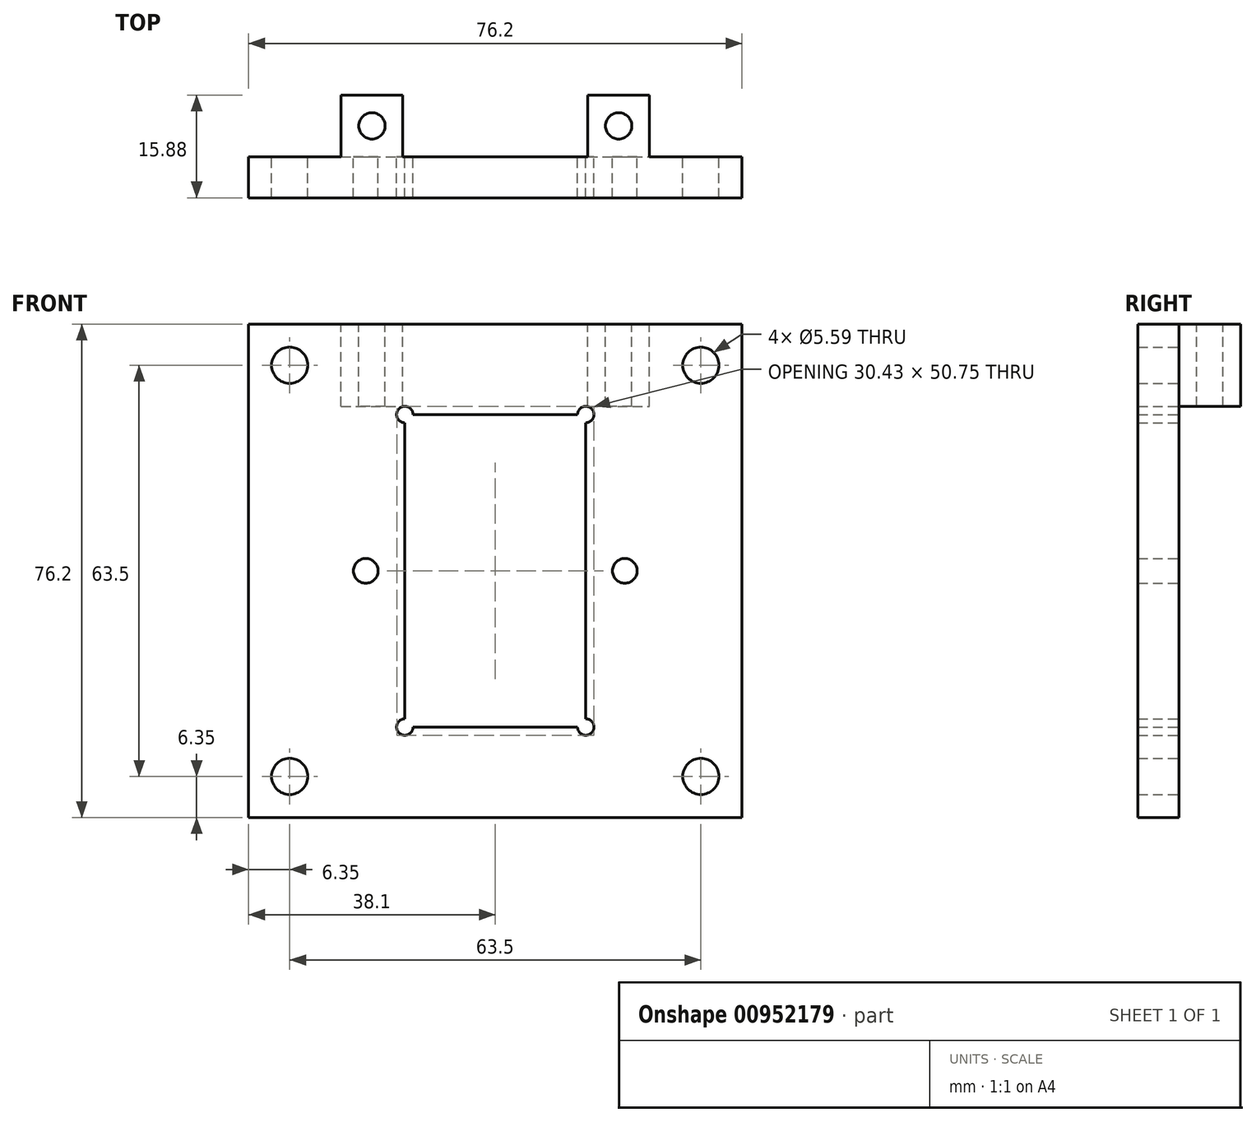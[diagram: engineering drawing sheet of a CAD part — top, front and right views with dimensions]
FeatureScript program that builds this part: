
annotation { "Feature Type Name" : "Feature", "Feature Type Description" : "" }
export const myFeature = defineFeature(function(context is Context, id is Id, definition is map)
    precondition{}
    {
        {
            var Q0;
            Q0=qCreatedBy(makeId("Front.planeOp"),FACE);
            var sketch = newSketch(context, id + "F0", { "sketchPlane" : qUnion([Q0])});
            skLineSegment(sketch, "E0.bottom", {"start": v(39.15, -38.1) * mm, "end": v(38.1, -38.1) * mm});
            skLineSegment(sketch, "E0.top", {"start": v(-38.1, 38.1) * mm, "end": v(38.1, 38.1) * mm});
            skLineSegment(sketch, "E0.right", {"start": v(38.1, -38.1) * mm, "end": v(38.1, 38.1) * mm});
            skLineSegment(sketch, "E1", {"start": v(-38.1, 38.1) * mm, "end": v(-38.1, -38.1) * mm});
            skLineSegment(sketch, "E2", {"start": v(38.1, -38.1) * mm, "end": v(-38.1, -38.1) * mm});
            skSolve(sketch);
        }
        {
            var Q0;
            Q0=qCreatedBy(makeId("Front.planeOp"),FACE);
            var sketch = newSketch(context, id + "F1", { "sketchPlane" : qUnion([Q0])});
            skLineSegment(sketch, "E3.bottom", {"start": v(-12.7, 24.13) * mm, "end": v(12.7, 24.13) * mm});
            skLineSegment(sketch, "E3.top", {"start": v(-12.7, -24.13) * mm, "end": v(12.7, -24.13) * mm});
            skLineSegment(sketch, "E3.left", {"start": v(-13.97, 22.86) * mm, "end": v(-13.97, -22.86) * mm});
            skLineSegment(sketch, "E3.right", {"start": v(13.97, 22.86) * mm, "end": v(13.97, -22.86) * mm});
            skArc(sketch, "E4", {"start": v(-12.7, 24.13) * mm, "mid": v(-14.87, 25.03) * mm, "end": v(-13.97, 22.86) * mm});
            skArc(sketch, "E5", {"start": v(13.97, 22.86) * mm, "mid": v(14.87, 25.03) * mm, "end": v(12.7, 24.13) * mm});
            skArc(sketch, "E6", {"start": v(-13.97, -22.86) * mm, "mid": v(-14.87, -25.03) * mm, "end": v(-12.7, -24.13) * mm});
            skArc(sketch, "E7", {"start": v(12.7, -24.13) * mm, "mid": v(14.87, -25.03) * mm, "end": v(13.97, -22.86) * mm});
            skSolve(sketch);
        }
        {
            var Q0;
            Q0=qCreatedBy(makeId("Front.planeOp"),FACE);
            var sketch = newSketch(context, id + "F2", { "sketchPlane" : qUnion([Q0])});
            skCircle(sketch, "E8", {"center": v(-31.75, 31.75) * mm, "radius": 2.8 * mm});
            skCircle(sketch, "E9", {"center": v(-31.75, -31.75) * mm, "radius": 2.8 * mm});
            skCircle(sketch, "E10", {"center": v(31.75, -31.75) * mm, "radius": 2.8 * mm});
            skCircle(sketch, "E11", {"center": v(31.75, 31.75) * mm, "radius": 2.8 * mm});
            skSolve(sketch);
        }
        {
            var Q0;
            Q0=qSketchRegion(id+"F0",true);
            extrude(context, id + "F3", {"entities" : qUnion([Q0]), "depth" : 6.35 * mm, "offsetDistance" : 25.4 * mm});
        }
        {
            var Q0;
            Q0=qSketchRegion(id+"F1",true);
            extrude(context, id + "F4", {"entities" : qUnion([Q0]), "operationType" : NewBodyOperationType.REMOVE, "endBound" : BoundingType.THROUGH_ALL, "depth" : 25.4 * mm, "offsetDistance" : 25.4 * mm});
        }
        {
            var Q0;
            Q0=qSketchRegion(id+"F2",true);
            extrude(context, id + "F5", {"entities" : qUnion([Q0]), "operationType" : NewBodyOperationType.REMOVE, "endBound" : BoundingType.THROUGH_ALL, "depth" : 25.4 * mm, "offsetDistance" : 25.4 * mm});
        }
        {
            var Q0;
            Q0=makeQuery(id+"F3.opExtrude","SWEPT_FACE",FACE,{"disambiguationData":[OSD([sQuery(id+"F0.wireOp",EDGE,"E0.top")])]});
            var sketch = newSketch(context, id + "F6", { "sketchPlane" : qUnion([Q0])});
            skLineSegment(sketch, "E12.bottom", {"start": v(-23.81, 0) * mm, "end": v(-14.29, 0) * mm});
            skLineSegment(sketch, "E12.top", {"start": v(-23.81, 9.53) * mm, "end": v(-14.29, 9.53) * mm});
            skLineSegment(sketch, "E12.left", {"start": v(-23.81, 0) * mm, "end": v(-23.81, 9.53) * mm});
            skLineSegment(sketch, "E12.right", {"start": v(-14.29, 0) * mm, "end": v(-14.29, 9.52) * mm});
            skLineSegment(sketch, "E13.bottom", {"start": v(23.81, 0) * mm, "end": v(14.29, 0) * mm});
            skLineSegment(sketch, "E13.top", {"start": v(23.81, 9.53) * mm, "end": v(14.29, 9.52) * mm});
            skLineSegment(sketch, "E13.left", {"start": v(23.81, 0) * mm, "end": v(23.81, 9.53) * mm});
            skLineSegment(sketch, "E13.right", {"start": v(14.29, 0) * mm, "end": v(14.29, 9.52) * mm});
            skCircle(sketch, "E14", {"center": v(-19.05, 4.76) * mm, "radius": 2.03 * mm});
            skCircle(sketch, "E15", {"center": v(19.05, 4.76) * mm, "radius": 2.03 * mm});
            skSolve(sketch);
        }
        {
            var Q0;
            Q0=qSketchRegion(id+"F6",true);
            extrude(context, id + "F7", {"entities" : qUnion([Q0]), "operationType" : NewBodyOperationType.ADD, "oppositeDirection" : true, "depth" : 12.7 * mm, "offsetDistance" : 25.4 * mm});
        }
        {
            var Q0;
            Q0=qCreatedBy(makeId("Front.planeOp"),FACE);
            var sketch = newSketch(context, id + "F8", { "sketchPlane" : qUnion([Q0])});
            skCircle(sketch, "E16", {"center": v(-20, 0) * mm, "radius": 1.9 * mm});
            skCircle(sketch, "E17", {"center": v(20, 0) * mm, "radius": 1.9 * mm});
            skSolve(sketch);
        }
        {
            var Q0;
            Q0 = qSketchRegion(id + "F8", true);
            extrude(context, id + "F9", {"entities" : qUnion([Q0]), "operationType" : NewBodyOperationType.REMOVE, "endBound" : BoundingType.THROUGH_ALL, "depth" : 25.4 * mm, "offsetDistance" : 25.4 * mm});
        }
    });
